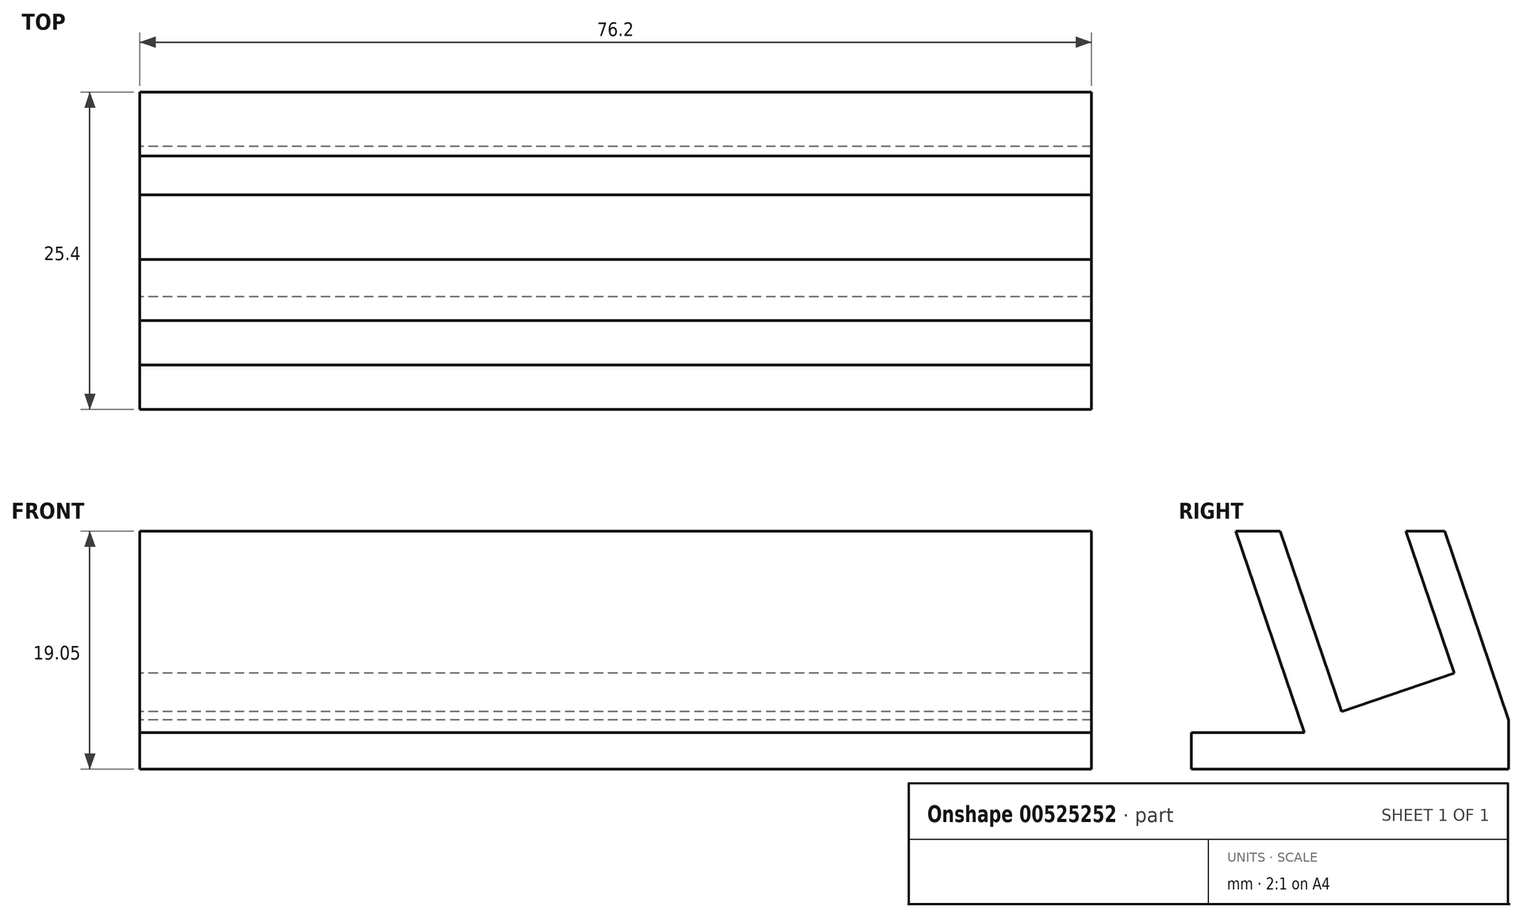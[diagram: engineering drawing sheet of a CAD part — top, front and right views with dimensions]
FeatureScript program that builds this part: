
annotation { "Feature Type Name" : "Feature", "Feature Type Description" : "" }
export const myFeature = defineFeature(function(context is Context, id is Id, definition is map)
    precondition{}
    {
        {
            var Q0;
            Q0=qCreatedBy(makeId("Top.planeOp"),FACE);
            var sketch = newSketch(context, id + "F0", { "sketchPlane" : qUnion([Q0])});
            skLineSegment(sketch, "E0", {"start": v(-37.32, 13.1) * mm, "end": v(38.88, 13.1) * mm});
            skLineSegment(sketch, "E1", {"start": v(38.88, 13.1) * mm, "end": v(38.88, -12.3) * mm});
            skLineSegment(sketch, "E2", {"start": v(38.88, -12.3) * mm, "end": v(-37.32, -12.3) * mm});
            skLineSegment(sketch, "E3", {"start": v(-37.32, -12.3) * mm, "end": v(-37.32, 13.1) * mm});
            skSolve(sketch);
        }
        {
            var Q0;
            Q0=makeQuery(id+"F0.imprint","IMPRINT",FACE,{"disambiguationData":[TD([[makeQuery(id+"F0.imprint","IMPRINT",EDGE,{"derivedFrom":sQuery(id+"F0.wireOp",EDGE,"E0")}),-1.0]])]});
            extrude(context, id + "F1", {"entities" : qUnion([Q0]), "depth" : 19.05 * mm, "offsetDistance" : 25.4 * mm});
        }
        {
            var Q0;
            Q0=makeQuery(id+"F1.opExtrude","SWEPT_FACE",FACE,{"disambiguationData":[OSD([sQuery(id+"F0.wireOp",EDGE,"E3")])]});
            var sketch = newSketch(context, id + "F2", { "sketchPlane" : qUnion([Q0])});
            skLineSegment(sketch, "E4", {"start": v(-4.87, 19.05) * mm, "end": v(-8.72, 7.68) * mm});
            skLineSegment(sketch, "E5", {"start": v(-8.72, 7.68) * mm, "end": v(0.3, 4.62) * mm});
            skLineSegment(sketch, "E6", {"start": v(0.3, 4.62) * mm, "end": v(5.2, 19.05) * mm});
            skLineSegment(sketch, "E7", {"start": v(-4.87, 19.05) * mm, "end": v(5.2, 19.05) * mm});
            skLineSegment(sketch, "E8", {"start": v(-7.96, 19.05) * mm, "end": v(-13.1, 3.93) * mm});
            skLineSegment(sketch, "E9", {"start": v(-13.1, 3.93) * mm, "end": v(-13.1, 19.05) * mm});
            skLineSegment(sketch, "E10", {"start": v(-13.1, 19.05) * mm, "end": v(-7.96, 19.05) * mm});
            skLineSegment(sketch, "E11", {"start": v(5.2, 19.05) * mm, "end": v(5.2, 4.62) * mm});
            skPoint(sketch, "E11.endSnap0", {"position": v(6.3, 4.62) * mm});
            skLineSegment(sketch, "E12", {"start": v(0.3, 4.62) * mm, "end": v(5.2, 4.62) * mm});
            skLineSegment(sketch, "E13", {"start": v(-7.96, 19.05) * mm, "end": v(-4.87, 19.05) * mm});
            skSolve(sketch);
        }
        {
            var Q0;
            Q0=makeQuery(id+"F2.imprint","IMPRINT",FACE,{"disambiguationData":[TD([[makeQuery(id+"F2.imprint","IMPRINT",EDGE,{"derivedFrom":sQuery(id+"F2.wireOp",EDGE,"E4")}),1.0]])]});
            extrude(context, id + "F3", {"entities" : qUnion([Q0]), "operationType" : NewBodyOperationType.REMOVE, "oppositeDirection" : true, "depth" : 76.2 * mm, "offsetDistance" : 25.4 * mm});
        }
        {
            var Q0;
            Q0=makeQuery(id+"F2.imprint","IMPRINT",FACE,{"disambiguationData":[TD([[makeQuery(id+"F2.imprint","IMPRINT",EDGE,{"derivedFrom":sQuery(id+"F2.wireOp",EDGE,"E8")}),-1.0]])]});
            extrude(context, id + "F4", {"entities" : qUnion([Q0]), "operationType" : NewBodyOperationType.REMOVE, "oppositeDirection" : true, "depth" : 76.2 * mm, "offsetDistance" : 25.4 * mm});
        }
        {
            var Q0;
            Q0=makeQuery(id+"F1.opExtrude","SWEPT_FACE",FACE,{"disambiguationData":[OSD([sQuery(id+"F0.wireOp",EDGE,"E3")])]});
            var sketch = newSketch(context, id + "F5", { "sketchPlane" : qUnion([Q0])});
            skLineSegment(sketch, "E14", {"start": v(8.75, 19.05) * mm, "end": v(3.28, 2.93) * mm});
            skLineSegment(sketch, "E15", {"start": v(3.28, 2.93) * mm, "end": v(12.3, 2.93) * mm});
            skLineSegment(sketch, "E16", {"start": v(8.5, 2.93) * mm, "end": v(8.5, 0) * mm});
            skLineSegment(sketch, "E17", {"start": v(-10.23, 12.36) * mm, "end": v(-7.45, 11.42) * mm});
            skLineSegment(sketch, "E18", {"start": v(0.3, 4.62) * mm, "end": v(-1.27, 0) * mm});
            skSolve(sketch);
        }
        {
            var Q0;
            Q0 = qSketchRegion(id + "F5", true);
            var Q1;
            {var subQ8=sQuery(id+"F5.wireOp",EDGE,"E14");Q1=makeQuery(id+"F5.imprint","IMPRINT",FACE,{"disambiguationData":[TD([[makeQuery(id+"F5.imprint","IMPRINT",EDGE,{"derivedFrom":subQ8}),1.0]])]});}
            extrude(context, id + "F6", {"entities" : qUnion([Q0, Q1]), "operationType" : NewBodyOperationType.REMOVE, "oppositeDirection" : true, "depth" : 76.2 * mm, "offsetDistance" : 25.4 * mm});
        }
    });
